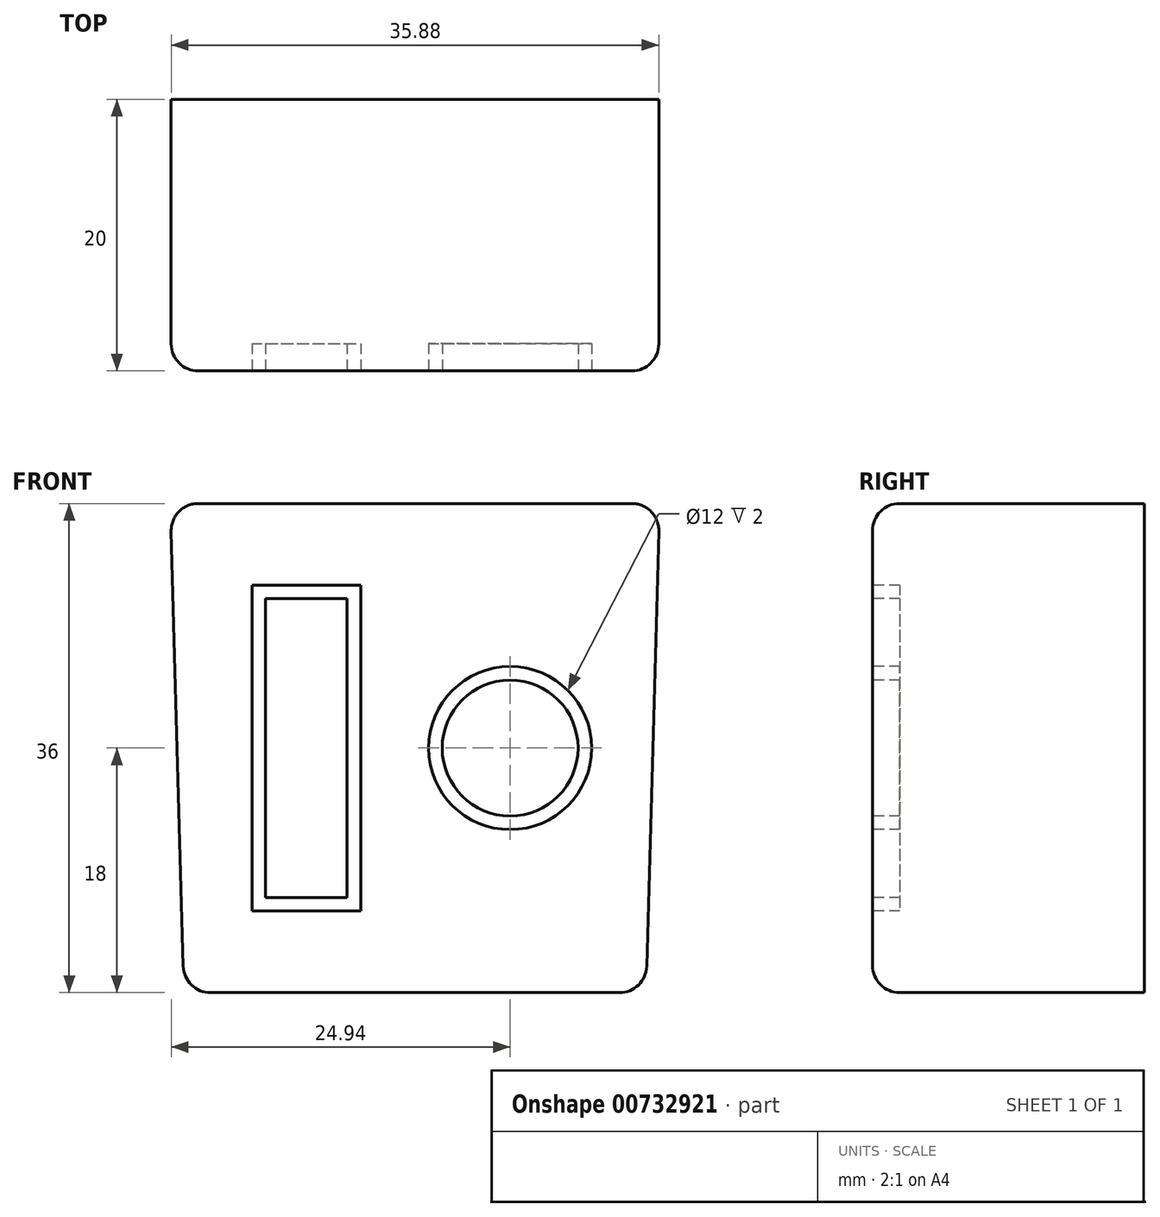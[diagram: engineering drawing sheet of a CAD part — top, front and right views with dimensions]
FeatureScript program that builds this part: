
annotation { "Feature Type Name" : "Feature", "Feature Type Description" : "" }
export const myFeature = defineFeature(function(context is Context, id is Id, definition is map)
    precondition{}
    {
        {
            var Q0;
            Q0=qCreatedBy(makeId("Front.planeOp"),FACE);
            var sketch = newSketch(context, id + "F0", { "sketchPlane" : qUnion([Q0])});
            skLineSegment(sketch, "E0.bottom", {"start": v(-18, 18) * mm, "end": v(18, 18) * mm});
            skLineSegment(sketch, "E0.top", {"start": v(-18, -18) * mm, "end": v(18, -18) * mm});
            skLineSegment(sketch, "E0.left", {"start": v(-18, 18) * mm, "end": v(-18, -18) * mm});
            skLineSegment(sketch, "E0.right", {"start": v(18, 18) * mm, "end": v(18, -18) * mm});
            skPoint(sketch, "E0.middle", {"position": v(0, 0) * mm});
            skLineSegment(sketch, "E1", {"start": v(-18, -18) * mm, "end": v(-17, -18) * mm});
            skLineSegment(sketch, "E2", {"start": v(-17, -18) * mm, "end": v(-18, 18) * mm});
            skLineSegment(sketch, "E3", {"start": v(18, -18) * mm, "end": v(17, -18) * mm});
            skLineSegment(sketch, "E4", {"start": v(17, -18) * mm, "end": v(18, 18) * mm});
            skSolve(sketch);
        }
        {
            var Q0;
            Q0=makeQuery(id+"F0.imprint","IMPRINT",FACE,{"disambiguationData":[TD([[makeQuery(id+"F0.imprint","IMPRINT",EDGE,{"derivedFrom":sQuery(id+"F0.wireOp",EDGE,"E0.bottom")}),-1.0]])]});
            extrude(context, id + "F1", {"entities" : qUnion([Q0]), "depth" : 20 * mm, "offsetDistance" : 25 * mm});
        }
        {
            var Q0;
            Q0=makeQuery(id+"F1.opExtrude","SWEPT_EDGE",EDGE,{"disambiguationData":[OSD([sQuery(id+"F0.wireOp",EDGE,"E0.top"),sQuery(id+"F0.wireOp",EDGE,"E2")])]});
            var Q1;
            Q1=makeQuery(id+"F1.opExtrude","SWEPT_EDGE",EDGE,{"disambiguationData":[OSD([sQuery(id+"F0.wireOp",EDGE,"E0.bottom"),sQuery(id+"F0.wireOp",EDGE,"E0.left"),sQuery(id+"F0.wireOp",EDGE,"E2")])]});
            var Q2;
            Q2=makeQuery(id+"F1.opExtrude","SWEPT_EDGE",EDGE,{"disambiguationData":[OSD([sQuery(id+"F0.wireOp",EDGE,"E0.bottom"),sQuery(id+"F0.wireOp",EDGE,"E0.right"),sQuery(id+"F0.wireOp",EDGE,"E4")])]});
            var Q3;
            Q3=makeQuery(id+"F1.opExtrude","SWEPT_EDGE",EDGE,{"disambiguationData":[OSD([sQuery(id+"F0.wireOp",EDGE,"E0.top"),sQuery(id+"F0.wireOp",EDGE,"E4")])]});
            var Q4;
            Q4=makeQuery(id+"F1.opExtrude","CAP_EDGE",EDGE,{"disambiguationData":[OSD([sQuery(id+"F0.wireOp",EDGE,"E4")])],"isStart":false});
            var Q5;
            Q5=makeQuery(id+"F1.opExtrude","CAP_EDGE",EDGE,{"disambiguationData":[OSD([sQuery(id+"F0.wireOp",EDGE,"E0.top")])],"isStart":false});
            var Q6;
            Q6=makeQuery(id+"F1.opExtrude","CAP_EDGE",EDGE,{"disambiguationData":[OSD([sQuery(id+"F0.wireOp",EDGE,"E2")])],"isStart":false});
            var Q7;
            Q7=makeQuery(id+"F1.opExtrude","CAP_EDGE",EDGE,{"disambiguationData":[OSD([sQuery(id+"F0.wireOp",EDGE,"E0.bottom")])],"isStart":false});
            fillet(context, id + "F2", {"entities" : qUnion([Q0, Q1, Q2, Q3, Q4, Q5, Q6, Q7]), "radius" : 2 * mm, "tangentPropagation" : true, "allowEdgeOverflow" : false});
        }
        {
            var Q0;
            Q0=makeQuery(id+"F1.opExtrude","CAP_FACE",FACE,{"disambiguationData":[OSD([sQuery(id+"F0.wireOp",EDGE,"E0.bottom"),sQuery(id+"F0.wireOp",EDGE,"E0.top"),sQuery(id+"F0.wireOp",EDGE,"E2"),sQuery(id+"F0.wireOp",EDGE,"E4")])],"isStart":false});
            var sketch = newSketch(context, id + "F3", { "sketchPlane" : qUnion([Q0])});
            skLineSegment(sketch, "E5", {"start": v(0, 0) * mm, "end": v(7, 0) * mm});
            skCircle(sketch, "E6", {"center": v(7, 0) * mm, "radius": 5 * mm});
            skCircle(sketch, "E7", {"center": v(7, 0) * mm, "radius": 6 * mm});
            skLineSegment(sketch, "E8", {"start": v(0, 0) * mm, "end": v(-8, 0) * mm});
            skLineSegment(sketch, "E9.bottom", {"start": v(-11, 11) * mm, "end": v(-5, 11) * mm});
            skLineSegment(sketch, "E9.top", {"start": v(-11, -11) * mm, "end": v(-5, -11) * mm});
            skLineSegment(sketch, "E9.left", {"start": v(-11, 11) * mm, "end": v(-11, -11) * mm});
            skLineSegment(sketch, "E9.right", {"start": v(-5, 11) * mm, "end": v(-5, -11) * mm});
            skPoint(sketch, "E9.middle", {"position": v(-8, 0) * mm});
            skLineSegment(sketch, "E10.bottom", {"start": v(-12, 12) * mm, "end": v(-4, 12) * mm});
            skLineSegment(sketch, "E10.top", {"start": v(-12, -12) * mm, "end": v(-4, -12) * mm});
            skLineSegment(sketch, "E10.left", {"start": v(-12, 12) * mm, "end": v(-12, -12) * mm});
            skLineSegment(sketch, "E10.right", {"start": v(-4, 12) * mm, "end": v(-4, -12) * mm});
            skSolve(sketch);
        }
        {
            var Q0;
            {var subQ1=sQuery(id+"F3.wireOp",EDGE,"E9.bottom");Q0=makeQuery(id+"F3.imprint","IMPRINT",FACE,{"disambiguationData":[TD([[makeQuery(id+"F3.imprint","IMPRINT",EDGE,{"derivedFrom":subQ1}),1.0]])]});}
            var Q1;
            Q1=makeQuery(id+"F3.imprint","IMPRINT",FACE,{"disambiguationData":[TD([[makeQuery(id+"F3.imprint","IMPRINT",EDGE,{"derivedFrom":sQuery(id+"F3.wireOp",EDGE,"E6")}),-1.0]])]});
            extrude(context, id + "F4", {"entities" : qUnion([Q0, Q1]), "operationType" : NewBodyOperationType.REMOVE, "oppositeDirection" : true, "depth" : 2 * mm, "offsetDistance" : 25 * mm});
        }
    });
